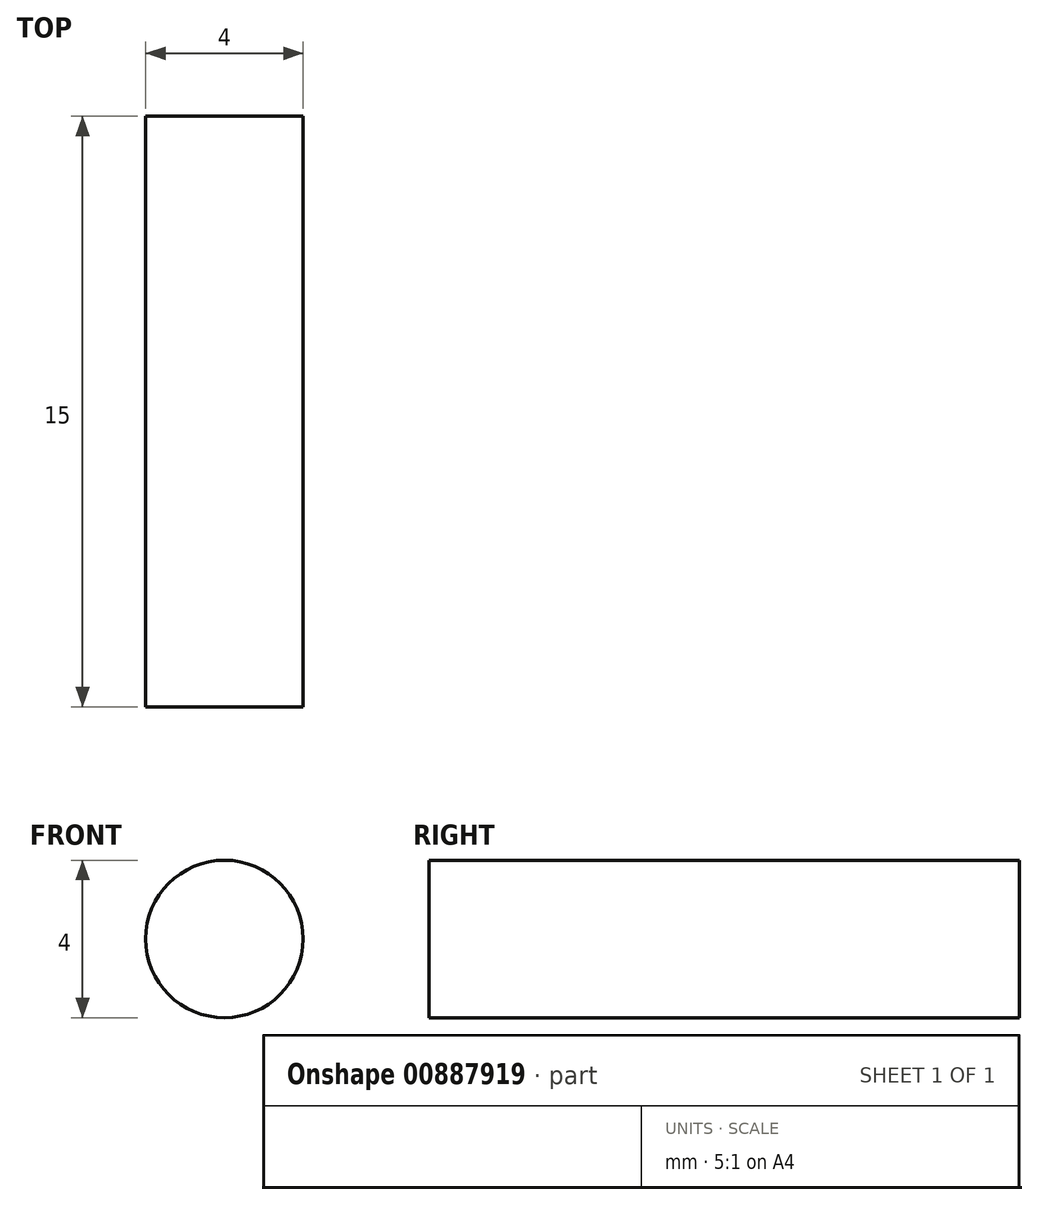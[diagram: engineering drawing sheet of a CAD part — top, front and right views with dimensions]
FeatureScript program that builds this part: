
annotation { "Feature Type Name" : "Feature", "Feature Type Description" : "" }
export const myFeature = defineFeature(function(context is Context, id is Id, definition is map)
    precondition{}
    {
        {
            var Q0;
            Q0=qCreatedBy(makeId("Front.planeOp"),FACE);
            var sketch = newSketch(context, id + "F0", { "sketchPlane" : qUnion([Q0])});
            skCircle(sketch, "E0", {"center": v(0, 0) * mm, "radius": 2 * mm});
            skSolve(sketch);
        }
        {
            var Q0;
            Q0 = qSketchRegion(id + "F0", true);
            extrude(context, id + "F1", {"entities" : qUnion([Q0]), "endBound" : BoundingType.SYMMETRIC, "depth" : 15 * mm, "offsetDistance" : 25 * mm});
        }
    });
